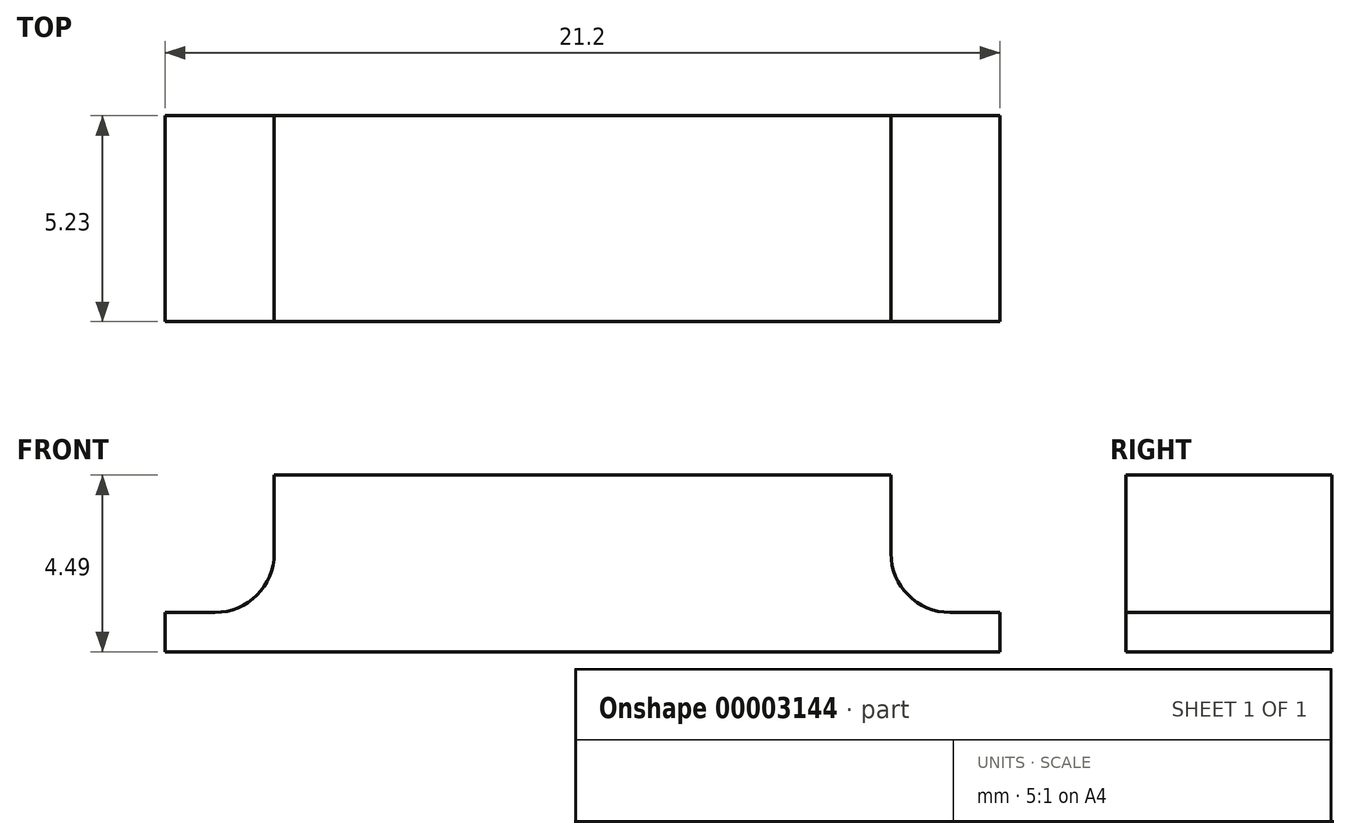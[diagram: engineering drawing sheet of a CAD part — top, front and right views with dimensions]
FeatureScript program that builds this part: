
annotation { "Feature Type Name" : "Feature", "Feature Type Description" : "" }
export const myFeature = defineFeature(function(context is Context, id is Id, definition is map)
    precondition{}
    {
        {
            var Q0;
            Q0=qCreatedBy(makeId("Front.planeOp"),FACE);
            var sketch = newSketch(context, id + "F0", { "sketchPlane" : qUnion([Q0])});
            skLineSegment(sketch, "E0", {"start": v(0, 10.25) * mm, "end": v(0, -11.27) * mm, "construction": true});
            skLineSegment(sketch, "E1", {"start": v(0, 0.66) * mm, "end": v(-7.84, 0.66) * mm});
            skLineSegment(sketch, "E2.0.MirrorCS", {"start": v(0, 0.66) * mm, "end": v(7.84, 0.66) * mm});
            skLineSegment(sketch, "E3", {"start": v(-7.84, 0.66) * mm, "end": v(-7.84, -1.33) * mm});
            skLineSegment(sketch, "E4", {"start": v(-9.34, -2.83) * mm, "end": v(-10.6, -2.83) * mm});
            skLineSegment(sketch, "E5", {"start": v(-10.6, -2.83) * mm, "end": v(-10.6, -3.83) * mm});
            skLineSegment(sketch, "E6", {"start": v(-10.6, -3.83) * mm, "end": v(0, -3.83) * mm});
            skLineSegment(sketch, "E7.0.MirrorCS", {"start": v(10.6, -3.83) * mm, "end": v(0, -3.83) * mm});
            skLineSegment(sketch, "E8.0.MirrorCS", {"start": v(9.34, -2.83) * mm, "end": v(10.6, -2.83) * mm});
            skLineSegment(sketch, "E8.1.MirrorCS", {"start": v(7.84, 0.66) * mm, "end": v(7.84, -1.33) * mm});
            skLineSegment(sketch, "E9.0.MirrorCS", {"start": v(10.6, -2.83) * mm, "end": v(10.6, -3.83) * mm});
            skPoint(sketch, "E10.visualSharp", {"position": v(-7.84, -2.83) * mm});
            skArc(sketch, "E10.filletArc", {"start": v(-9.34, -2.83) * mm, "mid": v(-8.27, -2.4) * mm, "end": v(-7.84, -1.33) * mm});
            skPoint(sketch, "E11.visualSharp", {"position": v(7.84, -2.83) * mm});
            skArc(sketch, "E11.filletArc", {"start": v(7.84, -1.33) * mm, "mid": v(8.27, -2.4) * mm, "end": v(9.34, -2.83) * mm});
            skSolve(sketch);
        }
        {
            var Q0;
            Q0=qSketchRegion(id+"F0",true);
            extrude(context, id + "F1", {"entities" : qUnion([Q0]), "depth" : 5.23 * mm});
        }
    });
